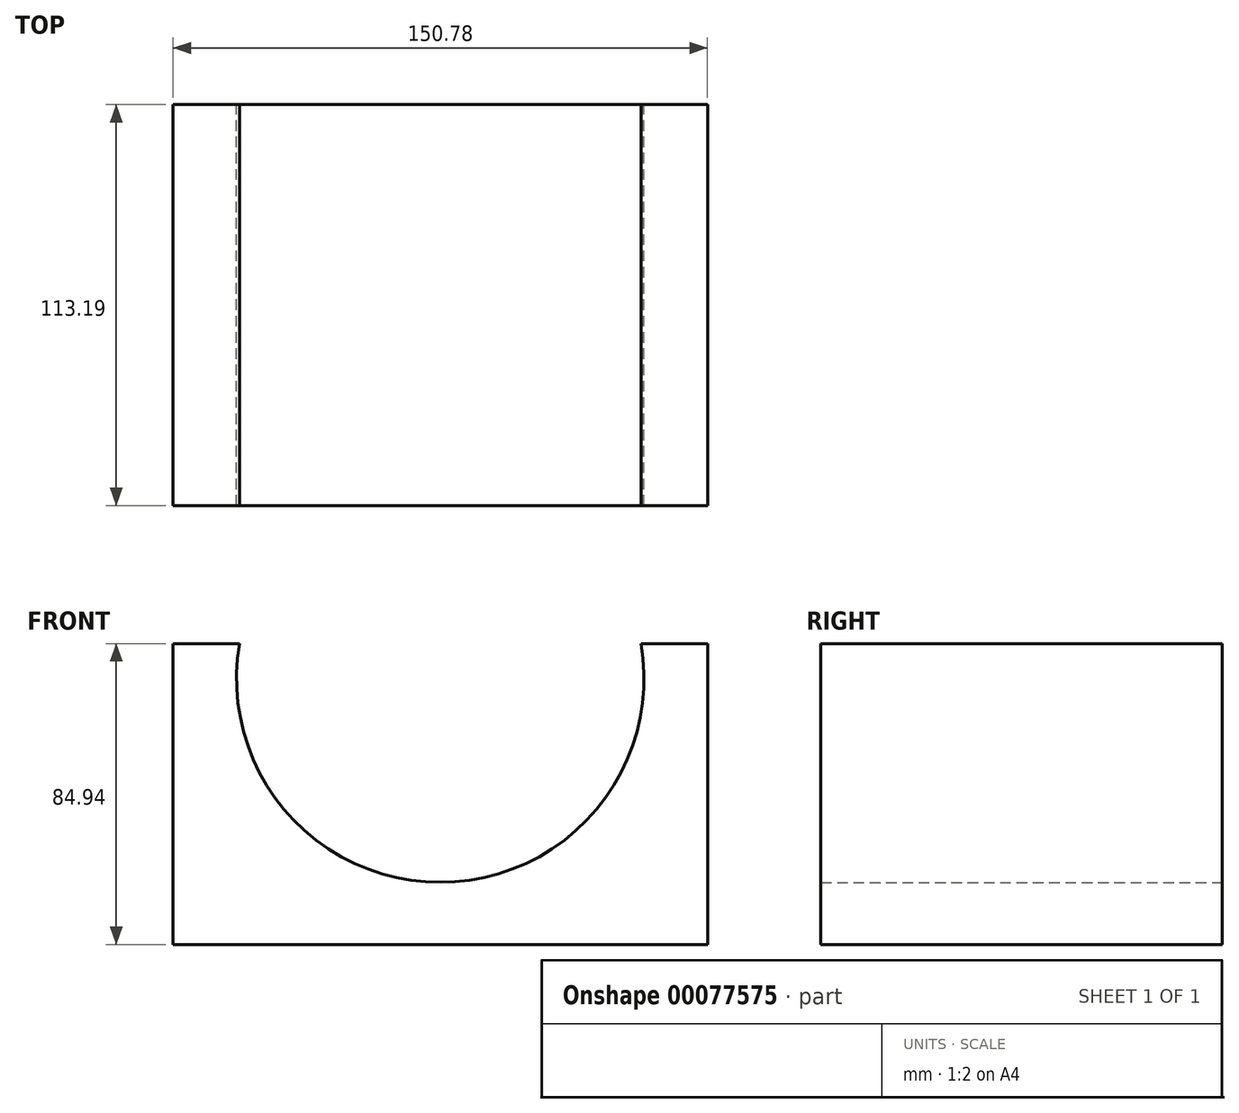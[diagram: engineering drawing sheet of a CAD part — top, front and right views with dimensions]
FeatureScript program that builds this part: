
annotation { "Feature Type Name" : "Feature", "Feature Type Description" : "" }
export const myFeature = defineFeature(function(context is Context, id is Id, definition is map)
    precondition{}
    {
        {
            var Q0;
            Q0=qCreatedBy(makeId("Front.planeOp"),FACE);
            var sketch = newSketch(context, id + "F0", { "sketchPlane" : qUnion([Q0])});
            skLineSegment(sketch, "E0.bottom", {"start": v(75.4, 42.47) * mm, "end": v(56.62, 42.47) * mm});
            skLineSegment(sketch, "E0.top", {"start": v(75.4, -42.47) * mm, "end": v(-75.4, -42.47) * mm});
            skLineSegment(sketch, "E0.left", {"start": v(75.4, 42.47) * mm, "end": v(75.4, -42.47) * mm});
            skLineSegment(sketch, "E0.right", {"start": v(-75.4, 42.47) * mm, "end": v(-75.4, -42.47) * mm});
            skPoint(sketch, "E0.middle", {"position": v(0, 0) * mm});
            skArc(sketch, "E1", {"start": v(-56.62, 42.47) * mm, "mid": v(0, -24.93) * mm, "end": v(56.62, 42.47) * mm});
            skLineSegment(sketch, "E2.trimOffspring", {"start": v(-56.62, 42.47) * mm, "end": v(-75.4, 42.47) * mm});
            skSolve(sketch);
        }
        {
            var Q0;
            Q0 = qSketchRegion(id + "F0", true);
            extrude(context, id + "F1", {"entities" : qUnion([Q0]), "depth" : 113.2 * mm});
        }
    });
